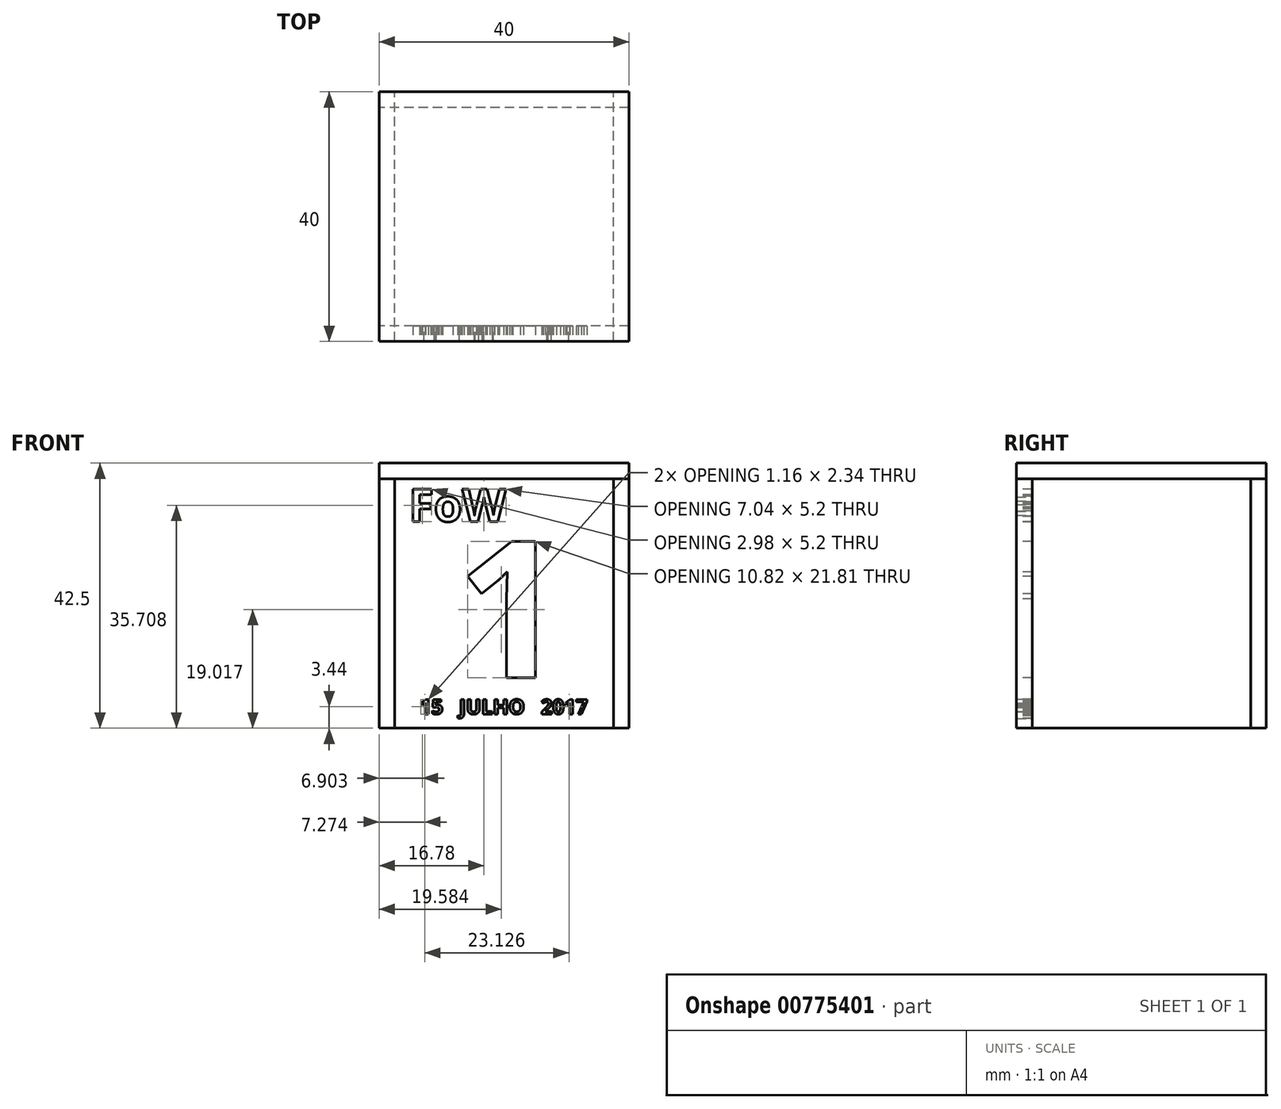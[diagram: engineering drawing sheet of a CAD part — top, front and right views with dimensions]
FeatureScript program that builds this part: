
annotation { "Feature Type Name" : "Feature", "Feature Type Description" : "" }
export const myFeature = defineFeature(function(context is Context, id is Id, definition is map)
    precondition{}
    {
        {
            var Q0;
            Q0=qCreatedBy(makeId("Top.planeOp"),FACE);
            var sketch = newSketch(context, id + "F0", { "sketchPlane" : qUnion([Q0])});
            skLineSegment(sketch, "E0.bottom", {"start": v(0, 0) * mm, "end": v(-40, 0) * mm});
            skLineSegment(sketch, "E0.top", {"start": v(0, 40) * mm, "end": v(-40, 40) * mm});
            skLineSegment(sketch, "E0.left", {"start": v(0, 0) * mm, "end": v(0, 40) * mm});
            skLineSegment(sketch, "E0.right", {"start": v(-40, 0) * mm, "end": v(-40, 40) * mm});
            skSolve(sketch);
        }
        {
            var Q0;
            Q0 = qSketchRegion(id + "F0", true);
            extrude(context, id + "F1", {"entities" : qUnion([Q0]), "depth" : 2.5 * mm, "offsetDistance" : 25 * mm});
        }
        {
            var Q0;
            Q0=makeQuery(id+"F1.opExtrude","SWEPT_FACE",FACE,{"disambiguationData":[OSD([sQuery(id+"F0.wireOp",EDGE,"E0.bottom")])]});
            var sketch = newSketch(context, id + "F2", { "sketchPlane" : qUnion([Q0])});
            skLineSegment(sketch, "E1.bottom", {"start": v(-40, 0) * mm, "end": v(0, 0) * mm});
            skLineSegment(sketch, "E1.top", {"start": v(-40, -40) * mm, "end": v(0, -40) * mm});
            skLineSegment(sketch, "E1.left", {"start": v(-40, 0) * mm, "end": v(-40, -40) * mm});
            skLineSegment(sketch, "E1.right", {"start": v(0, 0) * mm, "end": v(0, -40) * mm});
            skSolve(sketch);
        }
        {
            var Q0;
            Q0 = qSketchRegion(id + "F2", true);
            extrude(context, id + "F3", {"entities" : qUnion([Q0]), "oppositeDirection" : true, "depth" : 2.5 * mm, "offsetDistance" : 25 * mm});
        }
        {
            var Q0;
            Q0=makeQuery(id+"F1.opExtrude","SWEPT_FACE",FACE,{"disambiguationData":[OSD([sQuery(id+"F0.wireOp",EDGE,"E0.left")])]});
            var sketch = newSketch(context, id + "F4", { "sketchPlane" : qUnion([Q0])});
            skLineSegment(sketch, "E2.bottom", {"start": v(0, 0) * mm, "end": v(40, 0) * mm});
            skLineSegment(sketch, "E2.top", {"start": v(0, -40) * mm, "end": v(40, -40) * mm});
            skLineSegment(sketch, "E2.left", {"start": v(0, 0) * mm, "end": v(0, -40) * mm});
            skLineSegment(sketch, "E2.right", {"start": v(40, 0) * mm, "end": v(40, -40) * mm});
            skSolve(sketch);
        }
        {
            var Q0;
            Q0 = qSketchRegion(id + "F4", true);
            extrude(context, id + "F5", {"entities" : qUnion([Q0]), "oppositeDirection" : true, "depth" : 2.5 * mm, "offsetDistance" : 25 * mm});
        }
        {
            var Q0;
            Q0=makeQuery(id+"F1.opExtrude","SWEPT_FACE",FACE,{"disambiguationData":[OSD([sQuery(id+"F0.wireOp",EDGE,"E0.top")])]});
            var sketch = newSketch(context, id + "F6", { "sketchPlane" : qUnion([Q0])});
            skLineSegment(sketch, "E3.bottom", {"start": v(0, 0) * mm, "end": v(40, 0) * mm});
            skLineSegment(sketch, "E3.top", {"start": v(0, -40) * mm, "end": v(40, -40) * mm});
            skLineSegment(sketch, "E3.left", {"start": v(0, 0) * mm, "end": v(0, -40) * mm});
            skLineSegment(sketch, "E3.right", {"start": v(40, 0) * mm, "end": v(40, -40) * mm});
            skSolve(sketch);
        }
        {
            var Q0;
            Q0 = qSketchRegion(id + "F6", true);
            extrude(context, id + "F7", {"entities" : qUnion([Q0]), "oppositeDirection" : true, "depth" : 2.5 * mm, "offsetDistance" : 25 * mm});
        }
        {
            var Q0;
            Q0=makeQuery(id+"F1.opExtrude","SWEPT_FACE",FACE,{"disambiguationData":[OSD([sQuery(id+"F0.wireOp",EDGE,"E0.right")])]});
            var sketch = newSketch(context, id + "F8", { "sketchPlane" : qUnion([Q0])});
            skLineSegment(sketch, "E4.bottom", {"start": v(-40, 0) * mm, "end": v(0, 0) * mm});
            skLineSegment(sketch, "E4.top", {"start": v(-40, -40) * mm, "end": v(0, -40) * mm});
            skLineSegment(sketch, "E4.left", {"start": v(-40, 0) * mm, "end": v(-40, -40) * mm});
            skLineSegment(sketch, "E4.right", {"start": v(0, 0) * mm, "end": v(0, -40) * mm});
            skSolve(sketch);
        }
        {
            var Q0;
            Q0 = qSketchRegion(id + "F8", true);
            extrude(context, id + "F9", {"entities" : qUnion([Q0]), "oppositeDirection" : true, "depth" : 2.5 * mm, "offsetDistance" : 25 * mm});
        }
        {
            var Q0;
            Q0=makeQuery(id+"F3.opExtrude","CAP_FACE",FACE,{"disambiguationData":[OSD([sQuery(id+"F2.wireOp",EDGE,"E1.bottom"),sQuery(id+"F2.wireOp",EDGE,"E1.top"),sQuery(id+"F2.wireOp",EDGE,"E1.left"),sQuery(id+"F2.wireOp",EDGE,"E1.right")])],"isStart":true});
            var sketch = newSketch(context, id + "F10", { "sketchPlane" : qUnion([Q0])});
            skText(sketch, "E5", { "text": "FoW", "fontName": "OpenSans-Bold.ttf"});
            skText(sketch, "E6", { "text": "1", "fontName": "OpenSans-Bold.ttf"});
            skText(sketch, "E7", { "text": "15   JULHO   2017", "fontName": "OpenSans-Bold.ttf"});
            const initialGuessF10  = {"E5": [-0.03524, -0.00689, 1, 0, 0.00524], "E6": [-0.02763, -0.03189, 1, 0, 0.022], "E7": [-0.0335, -0.03773, 1, 0, 0.00236]};
            skSetInitialGuess(sketch, initialGuessF10);
            skSolve(sketch);
        }
        {
            var Q0;
            Q0 = qSketchRegion(id + "F10", true);
            extrude(context, id + "F11", {"entities" : qUnion([Q0]), "operationType" : NewBodyOperationType.REMOVE, "oppositeDirection" : true, "depth" : 3 * mm, "offsetDistance" : 25 * mm});
        }
    });
